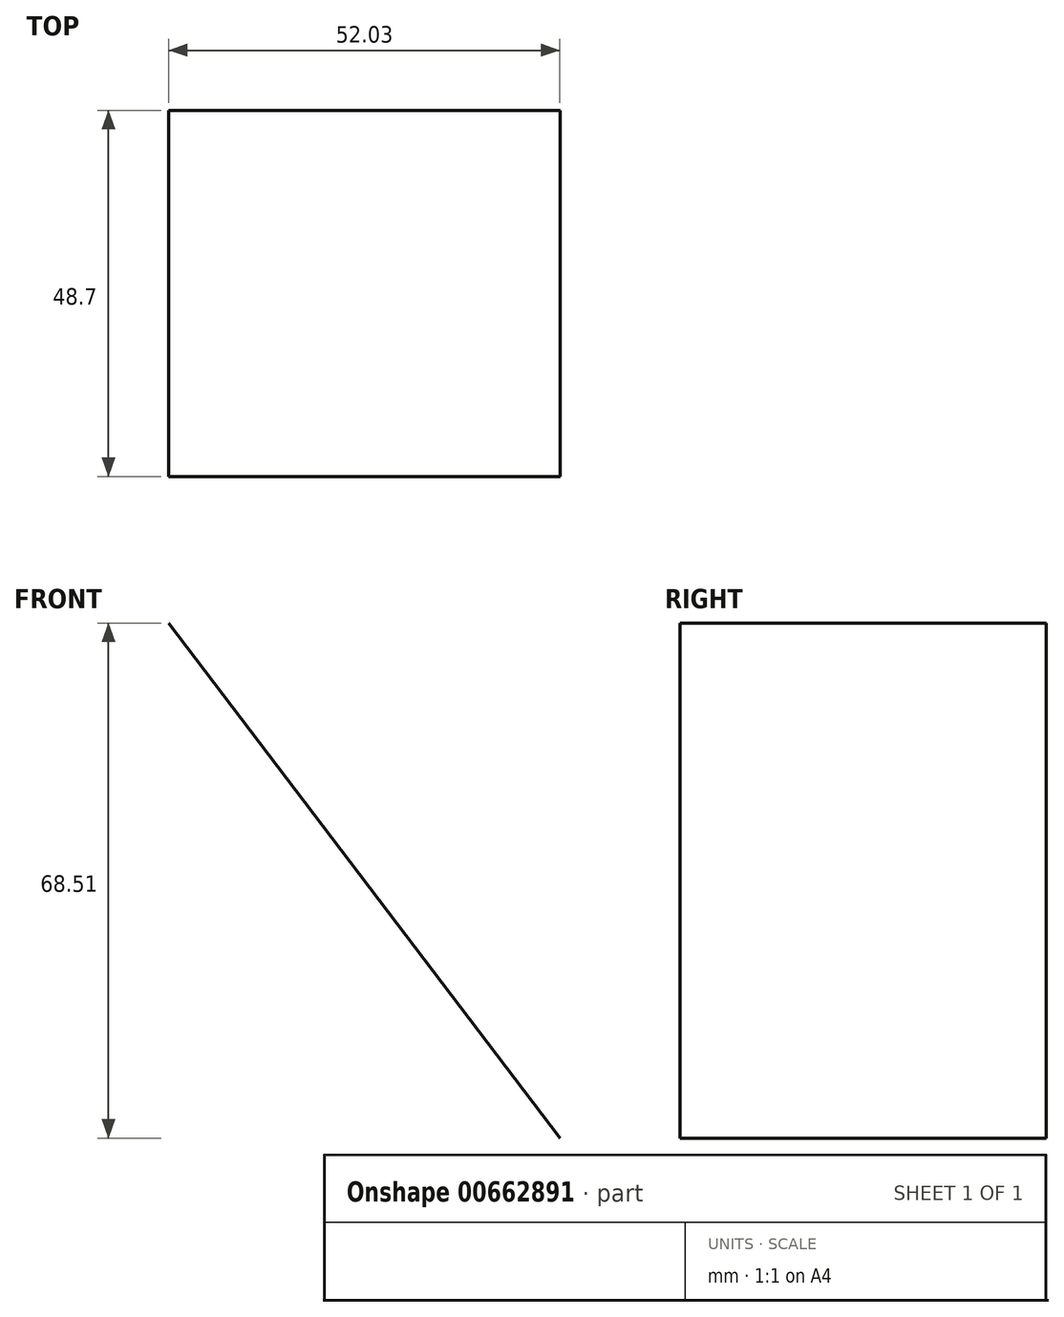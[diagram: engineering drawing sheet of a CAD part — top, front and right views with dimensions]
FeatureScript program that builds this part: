
annotation { "Feature Type Name" : "Feature", "Feature Type Description" : "" }
export const myFeature = defineFeature(function(context is Context, id is Id, definition is map)
    precondition{}
    {
        {
            var Q0;
            Q0=qCreatedBy(makeId("Front.planeOp"),FACE);
            var sketch = newSketch(context, id + "F0", { "sketchPlane" : qUnion([Q0])});
            skLineSegment(sketch, "E0", {"start": v(-114.08, 25.1) * mm, "end": v(-62.05, -43.42) * mm});
            skSolve(sketch);
        }
        {
            var Q0;
            Q0=sQuery(id+"F0.wireOp",EDGE,"E0");
            extrude(context, id + "F1", {"bodyType" : ToolBodyType.SURFACE, "surfaceEntities" : qUnion([Q0]), "depth" : 48.7 * mm, "offsetDistance" : 25 * mm});
        }
    });
